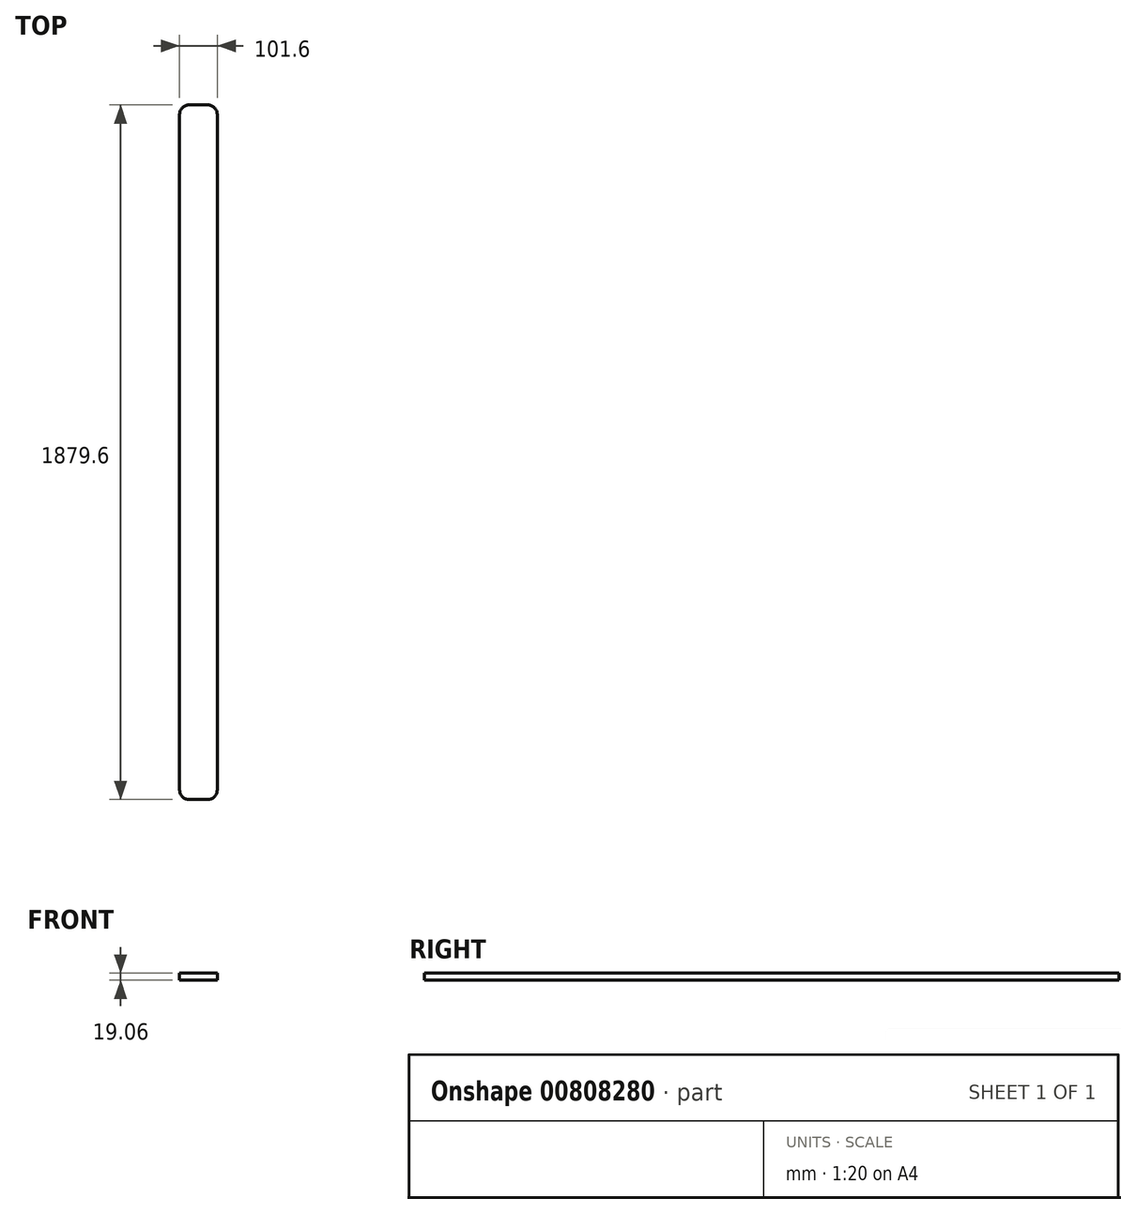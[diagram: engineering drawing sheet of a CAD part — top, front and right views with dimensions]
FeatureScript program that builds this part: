
annotation { "Feature Type Name" : "Feature", "Feature Type Description" : "" }
export const myFeature = defineFeature(function(context is Context, id is Id, definition is map)
    precondition{}
    {
        {
            var Q0;
            Q0=qCreatedBy(makeId("Top.planeOp"),FACE);
            var sketch = newSketch(context, id + "F0", { "sketchPlane" : qUnion([Q0])});
            skLineSegment(sketch, "E0.bottom", {"start": v(25.4, -939.8) * mm, "end": v(-25.4, -939.8) * mm});
            skLineSegment(sketch, "E0.top", {"start": v(25.4, 939.8) * mm, "end": v(-25.4, 939.8) * mm});
            skLineSegment(sketch, "E0.left", {"start": v(50.8, -914.4) * mm, "end": v(50.8, 914.4) * mm});
            skLineSegment(sketch, "E0.right", {"start": v(-50.8, -914.4) * mm, "end": v(-50.8, 914.4) * mm});
            skPoint(sketch, "E0.middle", {"position": v(0, 0) * mm});
            skPoint(sketch, "E1.visualSharp", {"position": v(-50.8, 939.8) * mm});
            skArc(sketch, "E1.filletArc", {"start": v(-25.4, 939.8) * mm, "mid": v(-43.36, 932.36) * mm, "end": v(-50.8, 914.4) * mm});
            skPoint(sketch, "E2.visualSharp", {"position": v(50.8, 939.8) * mm});
            skArc(sketch, "E2.filletArc", {"start": v(50.8, 914.4) * mm, "mid": v(43.36, 932.36) * mm, "end": v(25.4, 939.8) * mm, "construction": true});
            skPoint(sketch, "E3.visualSharp", {"position": v(50.8, -939.8) * mm});
            skArc(sketch, "E3.filletArc", {"start": v(25.4, -939.8) * mm, "mid": v(43.36, -932.36) * mm, "end": v(50.8, -914.4) * mm, "construction": true});
            skPoint(sketch, "E4.visualSharp", {"position": v(-50.8, -939.8) * mm});
            skArc(sketch, "E4.filletArc", {"start": v(-50.8, -914.4) * mm, "mid": v(-43.36, -932.36) * mm, "end": v(-25.4, -939.8) * mm});
            skArc(sketch, "E5", {"start": v(25.4, -939.8) * mm, "mid": v(43.36, -932.36) * mm, "end": v(50.8, -914.4) * mm});
            skArc(sketch, "E6", {"start": v(25.4, 939.8) * mm, "mid": v(43.36, 932.36) * mm, "end": v(50.8, 914.4) * mm});
            skSolve(sketch);
        }
        {
            var Q0;
            Q0=makeQuery(id+"F0.imprint","IMPRINT",FACE,{"disambiguationData":[TD([[makeQuery(id+"F0.imprint","IMPRINT",EDGE,{"derivedFrom":sQuery(id+"F0.wireOp",EDGE,"E0.bottom")}),-1.0]])]});
            extrude(context, id + "F1", {"entities" : qUnion([Q0]), "flatOperationType" : FlatOperationType.REMOVE, "depth" : 19.05 * mm, "offsetDistance" : 25.4 * mm, "domain" : OperationDomain.MODEL, "symmetric" : true});
        }
    });
